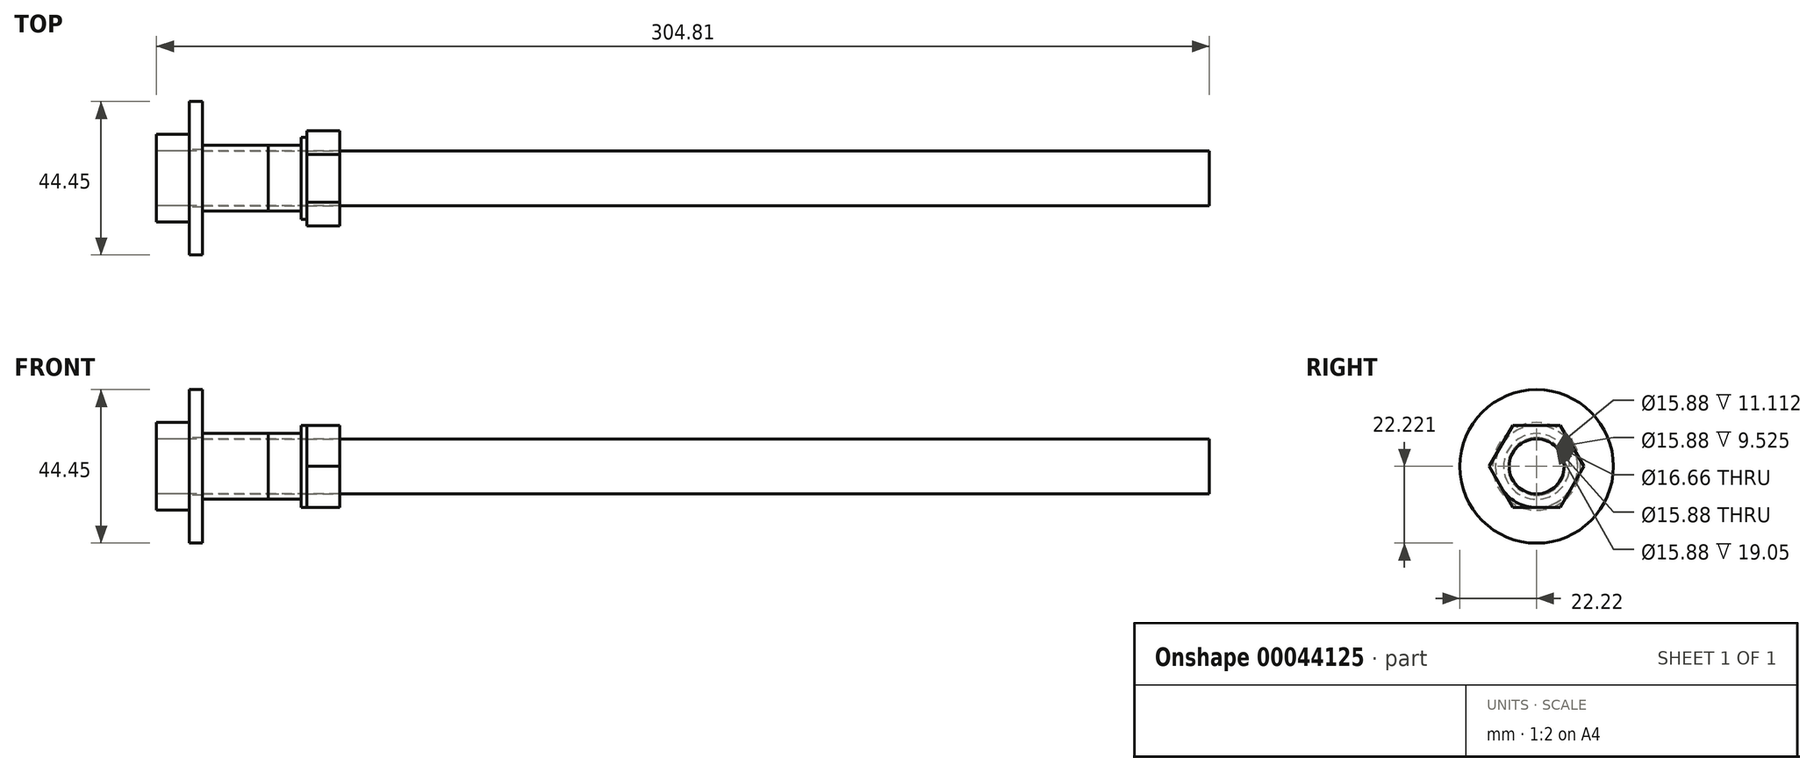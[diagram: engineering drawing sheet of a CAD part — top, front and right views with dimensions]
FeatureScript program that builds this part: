
annotation { "Feature Type Name" : "Feature", "Feature Type Description" : "" }
export const myFeature = defineFeature(function(context is Context, id is Id, definition is map)
    precondition{}
    {
        {
            var Q0;
            Q0=qCreatedBy(makeId("Right.planeOp"),FACE);
            var sketch = newSketch(context, id + "F0", { "sketchPlane" : qUnion([Q0])});
            skCircle(sketch, "E0", {"center": v(33.86, 47.48) * mm, "radius": 9.53 * mm});
            skSolve(sketch);
        }
        {
            var Q0;
            Q0=makeQuery(id+"F0.imprint","IMPRINT",FACE,{"disambiguationData":[TD([[makeQuery(id+"F0.imprint","IMPRINT",EDGE,{"derivedFrom":sQuery(id+"F0.wireOp",EDGE,"E0")}),1.0]])]});
            extrude(context, id + "F1", {"entities" : qUnion([Q0]), "depth" : 19.05 * mm});
        }
        {
            var Q0;
            Q0=makeQuery(id+"F1.opExtrude","CAP_FACE",FACE,{"disambiguationData":[OSD([sQuery(id+"F0.wireOp",EDGE,"E0")])],"isStart":false});
            var sketch = newSketch(context, id + "F2", { "sketchPlane" : qUnion([Q0])});
            skCircle(sketch, "E1", {"center": v(33.86, 47.48) * mm, "radius": 9.53 * mm});
            skSolve(sketch);
        }
        {
            var Q0;
            Q0 = qSketchRegion(id + "F2", true);
            extrude(context, id + "F3", {"entities" : qUnion([Q0]), "depth" : 9.52 * mm});
        }
        {
            var Q0;
            Q0=makeQuery(id+"F3.opExtrude","CAP_FACE",FACE,{"disambiguationData":[OSD([sQuery(id+"F2.wireOp",EDGE,"E1")])],"isStart":false});
            cPlane(context, id + "F4", {"entities" : qUnion([Q0]), "cplaneType" : CPlaneType.OFFSET, "offset" : 0 * mm, "width" : 152.4 * mm, "height" : 152.4 * mm});
        }
        {
            var Q0;
            Q0=qCreatedBy(id+"F4.planeOp",FACE);
            var sketch = newSketch(context, id + "F5", { "sketchPlane" : qUnion([Q0])});
            skCircle(sketch, "E2", {"center": v(33.86, 47.48) * mm, "radius": 11.9 * mm});
            skSolve(sketch);
        }
        {
            var Q0;
            Q0 = qSketchRegion(id + "F5", true);
            extrude(context, id + "F6", {"entities" : qUnion([Q0]), "operationType" : NewBodyOperationType.ADD, "depth" : 1.59 * mm});
        }
        {
            var Q0;
            Q0=makeQuery(id+"F6.opExtrude","CAP_FACE",FACE,{"disambiguationData":[OSD([sQuery(id+"F5.wireOp",EDGE,"E2")])],"isStart":false});
            var sketch = newSketch(context, id + "F7", { "sketchPlane" : qUnion([Q0])});
            skLineSegment(sketch, "E3", {"start": v(33.86, 47.48) * mm, "end": v(33.86, 59.39) * mm, "construction": true});
            skLineSegment(sketch, "E4", {"start": v(33.86, 47.48) * mm, "end": v(26.99, 59.39) * mm, "construction": true});
            skLineSegment(sketch, "E5", {"start": v(33.86, 59.39) * mm, "end": v(26.99, 59.39) * mm});
            skLineSegment(sketch, "E6.MirrorCS", {"start": v(33.86, 59.39) * mm, "end": v(40.73, 59.39) * mm});
            skLineSegment(sketch, "E7.1.0", {"start": v(23.55, 53.43) * mm, "end": v(26.99, 59.39) * mm});
            skLineSegment(sketch, "E7.1.1", {"start": v(23.55, 53.43) * mm, "end": v(20.11, 47.48) * mm});
            skLineSegment(sketch, "E7.2.0", {"start": v(23.55, 41.53) * mm, "end": v(20.11, 47.48) * mm});
            skLineSegment(sketch, "E7.2.1", {"start": v(23.55, 41.53) * mm, "end": v(26.99, 35.57) * mm});
            skLineSegment(sketch, "E7.3.0", {"start": v(33.86, 35.57) * mm, "end": v(26.99, 35.57) * mm});
            skLineSegment(sketch, "E7.3.1", {"start": v(33.86, 35.57) * mm, "end": v(40.73, 35.57) * mm});
            skLineSegment(sketch, "E7.4.0", {"start": v(44.17, 41.53) * mm, "end": v(40.73, 35.57) * mm});
            skLineSegment(sketch, "E7.4.1", {"start": v(44.17, 41.53) * mm, "end": v(47.6, 47.48) * mm});
            skLineSegment(sketch, "E7.5.0", {"start": v(44.17, 53.43) * mm, "end": v(47.6, 47.48) * mm});
            skLineSegment(sketch, "E7.5.1", {"start": v(44.17, 53.43) * mm, "end": v(40.73, 59.39) * mm});
            skPoint(sketch, "E7.center", {"position": v(33.86, 47.48) * mm});
            skSolve(sketch);
        }
        {
            var Q0;
            Q0 = qSketchRegion(id + "F7", true);
            extrude(context, id + "F8", {"entities" : qUnion([Q0]), "depth" : 9.52 * mm});
        }
        {
            var Q0;
            Q0=makeQuery(id+"F1.opExtrude","CAP_FACE",FACE,{"disambiguationData":[OSD([sQuery(id+"F0.wireOp",EDGE,"E0")])],"isStart":false});
            var sketch = newSketch(context, id + "F9", { "sketchPlane" : qUnion([Q0])});
            skCircle(sketch, "E8", {"center": v(33.86, 47.48) * mm, "radius": 7.94 * mm});
            skSolve(sketch);
        }
        {
            var Q0;
            Q0 = qSketchRegion(id + "F9", true);
            var Q1;
            Q1=makeQuery(id+"F1.opExtrude","CAP_FACE",FACE,{"disambiguationData":[OSD([sQuery(id+"F0.wireOp",EDGE,"E0")])],"isStart":true});
            var Q2;
            Q2=makeQuery(id+"F8.opExtrude","CAP_FACE",FACE,{"disambiguationData":[OSD([sQuery(id+"F7.wireOp",EDGE,"E5"),sQuery(id+"F7.wireOp",EDGE,"E6.MirrorCS"),sQuery(id+"F7.wireOp",EDGE,"E7.1.0"),sQuery(id+"F7.wireOp",EDGE,"E7.1.1"),sQuery(id+"F7.wireOp",EDGE,"E7.2.0"),sQuery(id+"F7.wireOp",EDGE,"E7.2.1"),sQuery(id+"F7.wireOp",EDGE,"E7.3.0"),sQuery(id+"F7.wireOp",EDGE,"E7.3.1"),sQuery(id+"F7.wireOp",EDGE,"E7.4.0"),sQuery(id+"F7.wireOp",EDGE,"E7.4.1"),sQuery(id+"F7.wireOp",EDGE,"E7.5.0"),sQuery(id+"F7.wireOp",EDGE,"E7.5.1")])],"isStart":false});
            extrude(context, id + "F10", {"entities" : qUnion([Q0]), "operationType" : NewBodyOperationType.REMOVE, "endBound" : BoundingType.THROUGH_ALL, "oppositeDirection" : true, "endBoundEntityFace" : qUnion([Q1]), "depth" : 25.4 * mm, "hasSecondDirection" : true, "secondDirectionBound" : SecondDirectionBoundingType.THROUGH_ALL, "secondDirectionOppositeDirection" : false, "secondDirectionBoundEntityFace" : qUnion([Q2]), "secondDirectionDepth" : 17.37 * mm});
        }
        {
            var Q0;
            Q0=qCreatedBy(makeId("Right.planeOp"),FACE);
            var sketch = newSketch(context, id + "F11", { "sketchPlane" : qUnion([Q0])});
            skCircle(sketch, "E9", {"center": v(33.86, 47.48) * mm, "radius": 22.23 * mm});
            skSolve(sketch);
        }
        {
            var Q0;
            Q0=makeQuery(id+"F11.imprint","IMPRINT",FACE,{"disambiguationData":[TD([[makeQuery(id+"F11.imprint","IMPRINT",EDGE,{"derivedFrom":sQuery(id+"F11.wireOp",EDGE,"E9")}),1.0]])]});
            extrude(context, id + "F12", {"entities" : qUnion([Q0]), "oppositeDirection" : true, "depth" : 3.8 * mm});
        }
        {
            var Q0;
            Q0=makeQuery(id+"F12.opExtrude","CAP_FACE",FACE,{"disambiguationData":[OSD([sQuery(id+"F11.wireOp",EDGE,"E9")])],"isStart":false});
            var sketch = newSketch(context, id + "F13", { "sketchPlane" : qUnion([Q0])});
            skCircle(sketch, "E10", {"center": v(-33.86, 47.48) * mm, "radius": 8.33 * mm});
            skSolve(sketch);
        }
        {
            var Q0;
            Q0 = qSketchRegion(id + "F13", true);
            var Q1;
            Q1=makeQuery(id+"F12.opExtrude","CAP_FACE",FACE,{"disambiguationData":[OSD([sQuery(id+"F11.wireOp",EDGE,"E9")])],"isStart":true});
            extrude(context, id + "F14", {"entities" : qUnion([Q0]), "operationType" : NewBodyOperationType.REMOVE, "endBound" : BoundingType.UP_TO_SURFACE, "oppositeDirection" : true, "endBoundEntityFace" : qUnion([Q1]), "depth" : 25.4 * mm});
        }
        {
            var Q0;
            Q0=makeQuery(id+"F12.opExtrude","CAP_FACE",FACE,{"disambiguationData":[OSD([sQuery(id+"F11.wireOp",EDGE,"E9")])],"isStart":false});
            var sketch = newSketch(context, id + "F15", { "sketchPlane" : qUnion([Q0])});
            skCircle(sketch, "E11", {"center": v(-33.86, 47.48) * mm, "radius": 12.7 * mm});
            skSolve(sketch);
        }
        {
            var Q0;
            Q0 = qSketchRegion(id + "F15", true);
            extrude(context, id + "F16", {"entities" : qUnion([Q0]), "depth" : 9.52 * mm});
        }
        {
            var Q0;
            Q0=makeQuery(id+"F16.opExtrude","CAP_FACE",FACE,{"disambiguationData":[OSD([sQuery(id+"F15.wireOp",EDGE,"E11")])],"isStart":false});
            var sketch = newSketch(context, id + "F17", { "sketchPlane" : qUnion([Q0])});
            skCircle(sketch, "E12", {"center": v(-33.86, 47.48) * mm, "radius": 7.94 * mm});
            skSolve(sketch);
        }
        {
            var Q0;
            Q0 = qSketchRegion(id + "F17", true);
            extrude(context, id + "F18", {"entities" : qUnion([Q0]), "operationType" : NewBodyOperationType.REMOVE, "endBound" : BoundingType.THROUGH_ALL, "oppositeDirection" : true, "depth" : 25.4 * mm});
        }
        {
            var Q0;
            Q0=makeQuery(id+"F16.opExtrude","CAP_FACE",FACE,{"disambiguationData":[OSD([sQuery(id+"F15.wireOp",EDGE,"E11")])],"isStart":false});
            var sketch = newSketch(context, id + "F19", { "sketchPlane" : qUnion([Q0])});
            skCircle(sketch, "E13", {"center": v(-33.86, 47.48) * mm, "radius": 7.94 * mm});
            skSolve(sketch);
        }
        {
            var Q0;
            Q0 = qSketchRegion(id + "F19", true);
            extrude(context, id + "F20", {"entities" : qUnion([Q0]), "oppositeDirection" : true, "depth" : 304.8 * mm});
        }
    });
